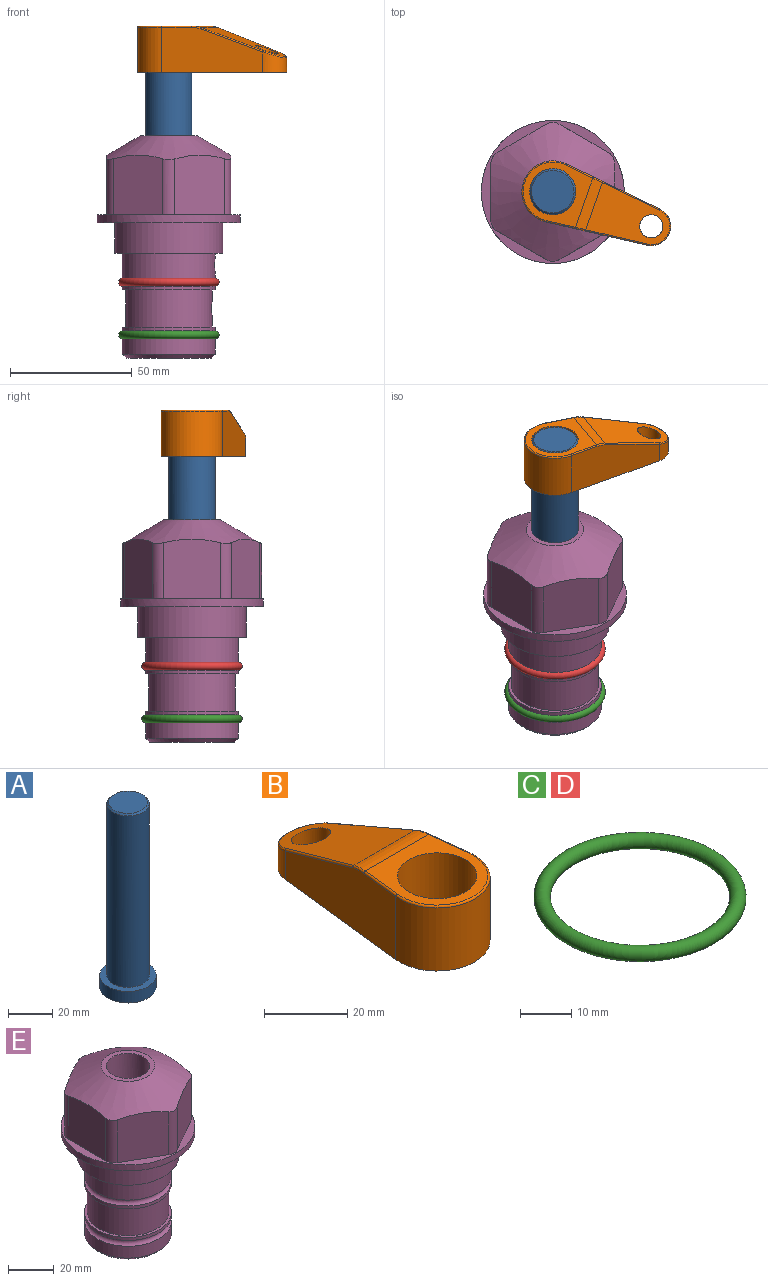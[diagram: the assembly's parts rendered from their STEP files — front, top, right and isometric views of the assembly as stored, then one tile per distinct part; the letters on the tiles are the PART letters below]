
ASSEMBLY  parts=5 mates=3
PART A: 6 faces, bbox 25.4x25.4x101.6 mm
  f0: plane 17.46x17.46mm, normal (0,0,1), area 239.5mm2, adj f5
  f1: plane 25.4x25.4mm, normal (0,0,-1), area 506.7mm2, adj f2
  f2: cylinder r=12.7mm len=25.4mm, axis (0,0,1), area 506.7mm2, adj f1,f3
  f3: plane 25.4x25.4mm, normal (0,0,1), area 221.7mm2, adj f2,f4
  f4: cylinder r=9.53mm len=94.46mm, axis (0,0,1), area 5653mm2, adj f3,f5
  f5: cone r=8.73mm half-angle=45deg, axis (0,0,-1), area 64.4mm2, adj f0,f4
PART B: 44 faces, bbox 27.5x64.5x19.1 mm
  f0: plane 2.3x0.95mm, normal (0,0,-1), area 1mm2, adj f25,f30,f34
  f1: plane 63.5x25.4mm, normal (0,0,-1), area 561.7mm2, adj f2,f3,f4,f5,f6,f7,f19,f20
  f2: cylinder r=12.7mm len=25.4mm, axis (0,0,-1), area 792.2mm2, adj f1,f3,f5,f13
  f3: plane 42.33x18.54mm, normal (0.99,0.11,0), area 647mm2, adj f1,f2,f4,f11,f12,f14
  f4: cylinder r=7.94mm len=15.78mm, axis (0,0,-1), area 158.6mm2, adj f1,f3,f5,f16
  f5: plane 42.33x18.54mm, normal (-0.99,0.11,0), area 647mm2, adj f1,f2,f4,f15,f17,f18
  f6: cylinder r=9.53mm len=19.05mm, axis (0,0,-1), area 1140.1mm2, adj f1,f8
  f7: cylinder r=4.76mm len=10.98mm, axis (0,0,-1), area 276.1mm2, adj f1,f9
  f8: plane 25.83x24.38mm, normal (0,0,1), area 262.2mm2, adj f6,f10,f11,f13,f15
  f9: plane 32.49x20.55mm, normal (0,0.34,0.94), area 489.9mm2, adj f7,f10,f14,f16,f18
  f10: cylinder r=12.7mm len=21.49mm, axis (-1,0,0), area 93.2mm2, adj f8,f9,f12,f17
  f11: cylinder r=0.51mm len=12.34mm, axis (0.11,-0.99,0), area 9.9mm2, adj f3,f8,f12,f13
  f12: bspline ~7.62x1.64mm, area 3.5mm2, adj f3,f10,f11,f14
  f13: torus R=12.19mm, axis (0,0,1), area 33.6mm2, adj f2,f8,f11,f15
  f14: cylinder r=0.51mm len=26.01mm, axis (0.1,-0.93,0.34), area 21.6mm2, adj f3,f9,f12,f16
  f15: cylinder r=0.51mm len=12.34mm, axis (0.11,0.99,0), area 9.9mm2, adj f5,f8,f13,f17
  f16: bspline ~15.78x7.05mm, area 15.7mm2, adj f4,f9,f14,f18
  f17: bspline ~7.62x1.64mm, area 3.5mm2, adj f5,f10,f15,f18
  f18: cylinder r=0.51mm len=26.01mm, axis (0.1,0.93,-0.34), area 21.6mm2, adj f5,f9,f16,f17
  f19: plane 21.6x14.29mm, normal (-0.99,-0.11,0), area 242.6mm2, adj f1,f26,f28,f34,f36,f38
  f20: plane 21.6x14.29mm, normal (0.99,-0.11,0), area 242.6mm2, adj f1,f27,f29,f37,f39,f41
  f21: cylinder r=12.7mm len=14.29mm, axis (0,0,-1), area 173.2mm2, adj f1,f26,f27,f30,f31,f33
  f22: cylinder r=7.94mm len=7.63mm, axis (0,0,-1), area 53.8mm2, adj f1,f28,f29,f42
  f23: plane 2.3x0.95mm, normal (0,0,-1), area 1mm2, adj f25,f33,f37
  f24: plane 17.94x12.32mm, normal (0,-0.34,-0.94), area 191.2mm2, adj f25,f38,f41,f42
  f25: cylinder r=9.53mm len=12.93mm, axis (-1,0,0), area 37.5mm2, adj f0,f23,f24,f31,f36,f39
  f26: cylinder r=1.59mm len=14.29mm, axis (0,0,-1), area 49mm2, adj f1,f19,f21,f32
  f27: cylinder r=1.59mm len=14.29mm, axis (0,0,-1), area 49mm2, adj f1,f20,f21,f35
  f28: cylinder r=1.59mm len=7.28mm, axis (0,0,-1), area 22.1mm2, adj f1,f19,f22,f40
  f29: cylinder r=1.59mm len=7.28mm, axis (0,0,-1), area 22.1mm2, adj f1,f20,f22,f43
  f30: torus R=14.29mm, axis (0,0,1), area 5.8mm2, adj f0,f21,f31,f32
  f31: bspline ~11.06x2.73mm, area 20.8mm2, adj f21,f25,f30,f33
  f32: sphere r=1.59mm, area 5.4mm2, adj f26,f30,f34
  f33: torus R=14.29mm, axis (0,0,1), area 5.8mm2, adj f21,f23,f31,f35
  f34: cylinder r=1.59mm len=1.68mm, axis (-0.11,0.99,0), area 2.4mm2, adj f0,f19,f32,f36
  f35: sphere r=1.59mm, area 5.4mm2, adj f27,f33,f37
  f36: bspline ~5.82x2.33mm, area 7.7mm2, adj f19,f25,f34,f38
  f37: cylinder r=1.59mm len=1.68mm, axis (0.11,0.99,0), area 2.4mm2, adj f20,f23,f35,f39
  f38: cylinder r=1.59mm len=18.33mm, axis (0.1,-0.93,0.34), area 46.7mm2, adj f19,f24,f36,f40
  f39: bspline ~5.82x2.33mm, area 7.7mm2, adj f20,f25,f37,f41
  f40: sphere r=1.59mm, area 3.6mm2, adj f28,f38,f42
  f41: cylinder r=1.59mm len=18.33mm, axis (0.1,0.93,-0.34), area 46.7mm2, adj f20,f24,f39,f43
  f42: bspline ~8.31x1.84mm, area 15.3mm2, adj f22,f24,f40,f43
  f43: sphere r=1.59mm, area 3.6mm2, adj f29,f41,f42
PART C: 1 faces, bbox 44.7x44.7x3.2 mm
  f0: torus R=19.05mm, axis (0,0,1), area 1193.9mm2
PART D: same geometry as C
PART E: 36 faces, bbox 58.7x58.7x91.2 mm
  f0: cylinder r=17.78mm len=35.56mm, axis (0,0,1), area 1670.8mm2, adj f23,f24,f31
  f1: cylinder r=19.05mm len=38.1mm, axis (0,0,1), area 1191.9mm2, adj f26,f27,f30
  f2: plane 58.66x58.66mm, normal (0,0,-1), area 1150.6mm2, adj f3,f28
  f3: cylinder r=29.33mm len=58.66mm, axis (0,0,-1), area 585.1mm2, adj f2,f4
  f4: plane 58.66x58.66mm, normal (0,0,1), area 475.9mm2, adj f3,f5,f6,f7,f8,f9,f10,f11
  f5: plane 24.5x20.32mm, normal (0.5,-0.87,0), area 562.8mm2, adj f4,f15,f16,f17
  f6: plane 24.5x20.32mm, normal (-0.5,-0.87,0), area 562.8mm2, adj f4,f14,f15,f17
  f7: plane 24.5x23.48mm, normal (-1,0,0), area 562.8mm2, adj f4,f13,f14,f17
  f8: plane 24.5x20.32mm, normal (-0.5,0.87,0), area 562.8mm2, adj f4,f12,f13,f17
  f9: plane 24.5x20.32mm, normal (0.5,0.87,0), area 562.8mm2, adj f4,f11,f12,f17
  f10: plane 24.5x23.48mm, normal (1,0,0), area 562.8mm2, adj f4,f11,f16,f17
  f11: cylinder r=5.08mm len=23.01mm, axis (0,0,-1), area 121.2mm2, adj f4,f9,f10,f17
  f12: cylinder r=5.08mm len=23.01mm, axis (0,0,-1), area 121.2mm2, adj f4,f8,f9,f17
  f13: cylinder r=5.08mm len=23.01mm, axis (0,0,-1), area 121.2mm2, adj f4,f7,f8,f17
  f14: cylinder r=5.08mm len=23.01mm, axis (0,0,-1), area 121.2mm2, adj f4,f6,f7,f17
  f15: cylinder r=5.08mm len=23.01mm, axis (0,0,-1), area 121.2mm2, adj f4,f5,f6,f17
  f16: cylinder r=5.08mm len=23.01mm, axis (0,0,-1), area 121.2mm2, adj f4,f5,f10,f17
  f17: cone r=11.73mm half-angle=60deg, axis (0,0,-1), area 2071.8mm2, adj f5,f6,f7,f8,f9,f10,f11,f12
  f18: plane 23.46x23.46mm, normal (0,0,1), area 147.4mm2, adj f17,f35
  f19: plane 34.93x34.93mm, normal (0,0,-1), area 958mm2, adj f29
  f20: cylinder r=19.05mm len=38.1mm, axis (0,0,1), area 760.1mm2, adj f21,f29
  f21: torus R=19.05mm, axis (0,0,1), area 565.3mm2, adj f20,f22
  f22: cylinder r=19.05mm len=38.1mm, axis (0,0,1), area 190mm2, adj f21,f23
  f23: plane 38.1x38.1mm, normal (0,0,1), area 146.9mm2, adj f0,f22
  f24: plane 38.1x38.1mm, normal (0,0,-1), area 146.9mm2, adj f0,f25
  f25: cylinder r=19.05mm len=38.1mm, axis (0,0,1), area 190mm2, adj f24,f26
  f26: torus R=19.05mm, axis (0,0,1), area 565.3mm2, adj f1,f25
  f27: plane 44.45x44.45mm, normal (0,0,-1), area 411.7mm2, adj f1,f28
  f28: cylinder r=22.23mm len=44.45mm, axis (0,0,1), area 1773.5mm2, adj f2,f27
  f29: cone r=19.05mm half-angle=45deg, axis (0,0,1), area 257.5mm2, adj f19,f20
  f30: cylinder r=3.17mm len=6.75mm, axis (-1,0,0), area 128mm2, adj f1,f33
  f31: cylinder r=3.17mm len=6.35mm, axis (-1,0,0), area 102.5mm2, adj f0,f33
  f32: plane 25.4x25.4mm, normal (0,0,1), area 506.7mm2, adj f33
  f33: cylinder r=12.7mm len=66.42mm, axis (0,0,-1), area 5236.2mm2, adj f30,f31,f32,f34
  f34: cone r=9.53mm half-angle=30deg, axis (0,0,-1), area 443.4mm2, adj f33,f35
  f35: cylinder r=9.53mm len=19.05mm, axis (0,0,-1), area 849mm2, adj f18,f34
PLACE A rot(axis=(0,0,-1),19.3deg) t=(0,0,7.04)mm
PLACE B rot(axis=(0,0,-1),109.3deg) t=(0,0,61.65)mm
PLACE C t=(0,0,-21.59)mm
PLACE D at identity
PLACE E at identity fixed
MATE fastened C.f0 <-> E.f0  axis (0,0,1) through (0,0,-46.1)mm
MATE cylindrical A.f2 <-> E.f0  axis (0,0,1) through (0,0,32.68)mm
MATE fastened B.f2 <-> A.f2  axis (0,0,1) through (0,0,80.7)mm
